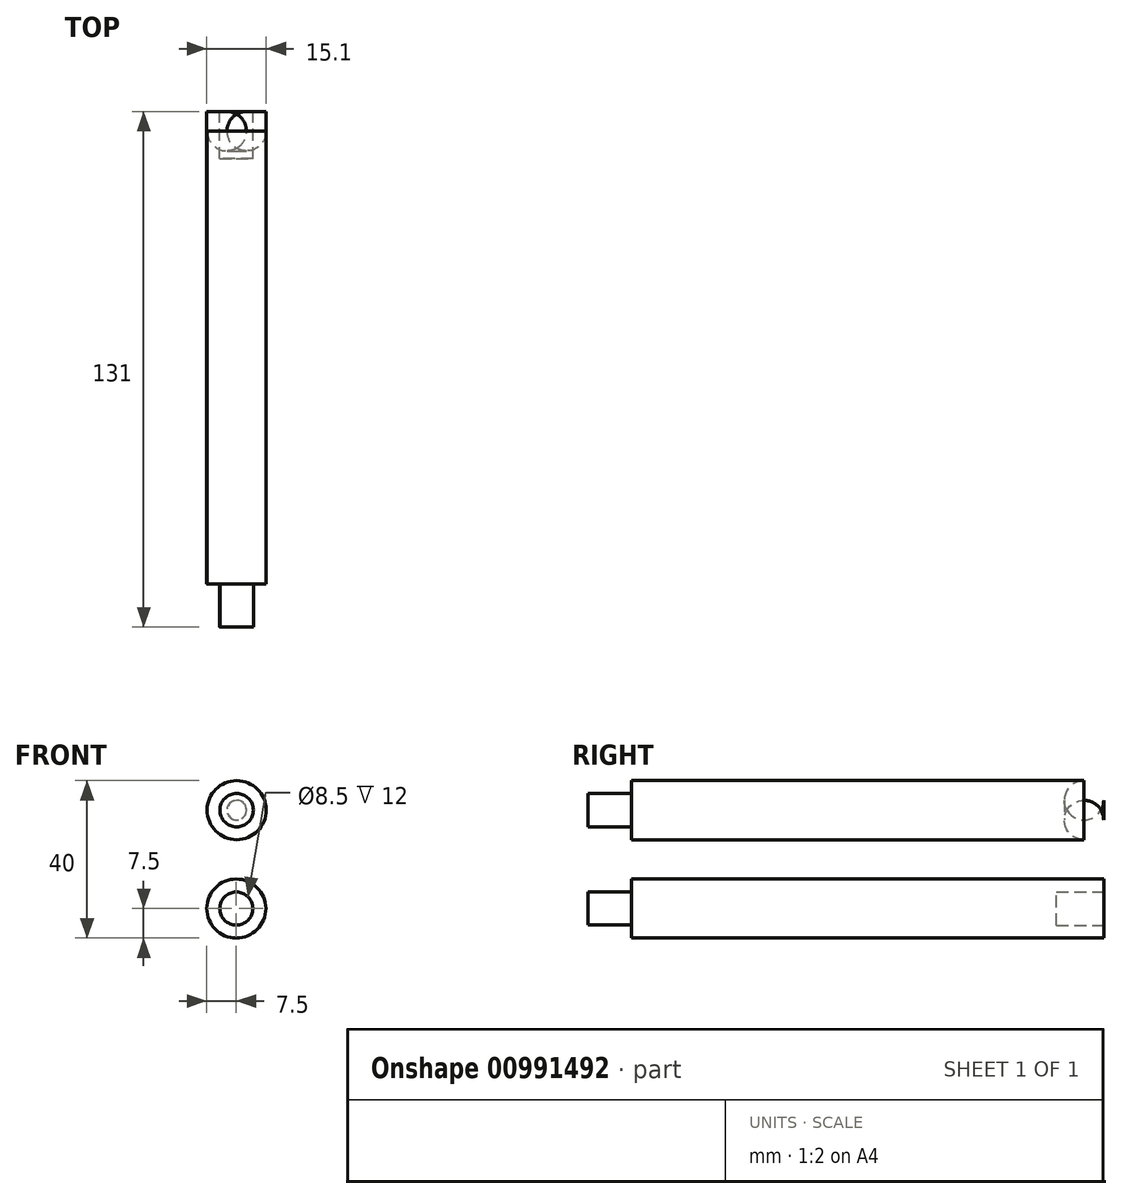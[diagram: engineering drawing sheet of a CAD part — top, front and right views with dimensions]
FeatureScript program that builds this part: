
annotation { "Feature Type Name" : "Feature", "Feature Type Description" : "" }
export const myFeature = defineFeature(function(context is Context, id is Id, definition is map)
    precondition{}
    {
        {
            var Q0;
            Q0=qCreatedBy(makeId("Front.planeOp"),FACE);
            var sketch = newSketch(context, id + "F0", { "sketchPlane" : qUnion([Q0])});
            skCircle(sketch, "E0", {"center": v(0, 0) * mm, "radius": 4.25 * mm});
            skCircle(sketch, "E1", {"center": v(0, 0) * mm, "radius": 7.5 * mm});
            skCircle(sketch, "E2", {"center": v(0.1, 25) * mm, "radius": 4.25 * mm});
            skCircle(sketch, "E3", {"center": v(0.1, 25) * mm, "radius": 7.5 * mm});
            skSolve(sketch);
        }
        {
            var Q0;
            Q0 = qSketchRegion(id + "F0", true);
            var Q1;
            Q1=makeQuery(id+"F0.imprint","IMPRINT",FACE,{"disambiguationData":[TD([[makeQuery(id+"F0.imprint","IMPRINT",EDGE,{"derivedFrom":sQuery(id+"F0.wireOp",EDGE,"E0")}),1.0]])]});
            var Q2;
            Q2=makeQuery(id+"F0.imprint","IMPRINT",FACE,{"disambiguationData":[TD([[makeQuery(id+"F0.imprint","IMPRINT",EDGE,{"derivedFrom":sQuery(id+"F0.wireOp",EDGE,"E2")}),1.0]])]});
            extrude(context, id + "F1", {"entities" : qUnion([Q0, Q1, Q2]), "depth" : 120 * mm, "offsetDistance" : 25 * mm});
        }
        {
            var Q0;
            Q0=qCreatedBy(makeId("Front.planeOp"),FACE);
            var sketch = newSketch(context, id + "F2", { "sketchPlane" : qUnion([Q0])});
            skCircle(sketch, "E4", {"center": v(0, 0) * mm, "radius": 4.25 * mm});
            skSolve(sketch);
        }
        {
            var Q0;
            Q0 = qSketchRegion(id + "F2", true);
            extrude(context, id + "F3", {"entities" : qUnion([Q0]), "operationType" : NewBodyOperationType.REMOVE, "depth" : 12 * mm, "offsetDistance" : 25 * mm});
        }
        {
            var Q0;
            Q0=makeQuery(id+"F1.opExtrude","CAP_FACE",FACE,{"disambiguationData":[OSD([sQuery(id+"F0.wireOp",EDGE,"E1")])],"isStart":false});
            var sketch = newSketch(context, id + "F4", { "sketchPlane" : qUnion([Q0])});
            skPoint(sketch, "E5.center.orphan", {"position": v(0, 0) * mm});
            skCircle(sketch, "E6", {"center": v(0, 0) * mm, "radius": 4.2 * mm});
            skSolve(sketch);
        }
        {
            var Q0;
            Q0 = qSketchRegion(id + "F4", true);
            extrude(context, id + "F5", {"entities" : qUnion([Q0]), "operationType" : NewBodyOperationType.ADD, "depth" : 11 * mm, "offsetDistance" : 25 * mm});
        }
        {
            var Q0;
            Q0=makeQuery(id+"F1.opExtrude","CAP_FACE",FACE,{"disambiguationData":[OSD([sQuery(id+"F0.wireOp",EDGE,"E3")])],"isStart":false});
            var sketch = newSketch(context, id + "F6", { "sketchPlane" : qUnion([Q0])});
            skCircle(sketch, "E7", {"center": v(0.1, 25) * mm, "radius": 4.25 * mm});
            skSolve(sketch);
        }
        {
            var Q0;
            Q0=makeQuery(id+"F6.imprint","IMPRINT",FACE,{"disambiguationData":[TD([[makeQuery(id+"F6.imprint","IMPRINT",EDGE,{"derivedFrom":sQuery(id+"F6.wireOp",EDGE,"E7")}),1.0]])]});
            extrude(context, id + "F7", {"entities" : qUnion([Q0]), "operationType" : NewBodyOperationType.ADD, "depth" : 11 * mm, "offsetDistance" : 25 * mm});
        }
        {
            var Q0;
            Q0=makeQuery(id+"F1.opExtrude","CAP_EDGE",EDGE,{"disambiguationData":[OSD([sQuery(id+"F0.wireOp",EDGE,"E3")])],"isStart":true});
            fillet(context, id + "F8", {"entities" : qUnion([Q0]), "radius" : 5 * mm, "tangentPropagation" : true, "allowEdgeOverflow" : false});
        }
    });
